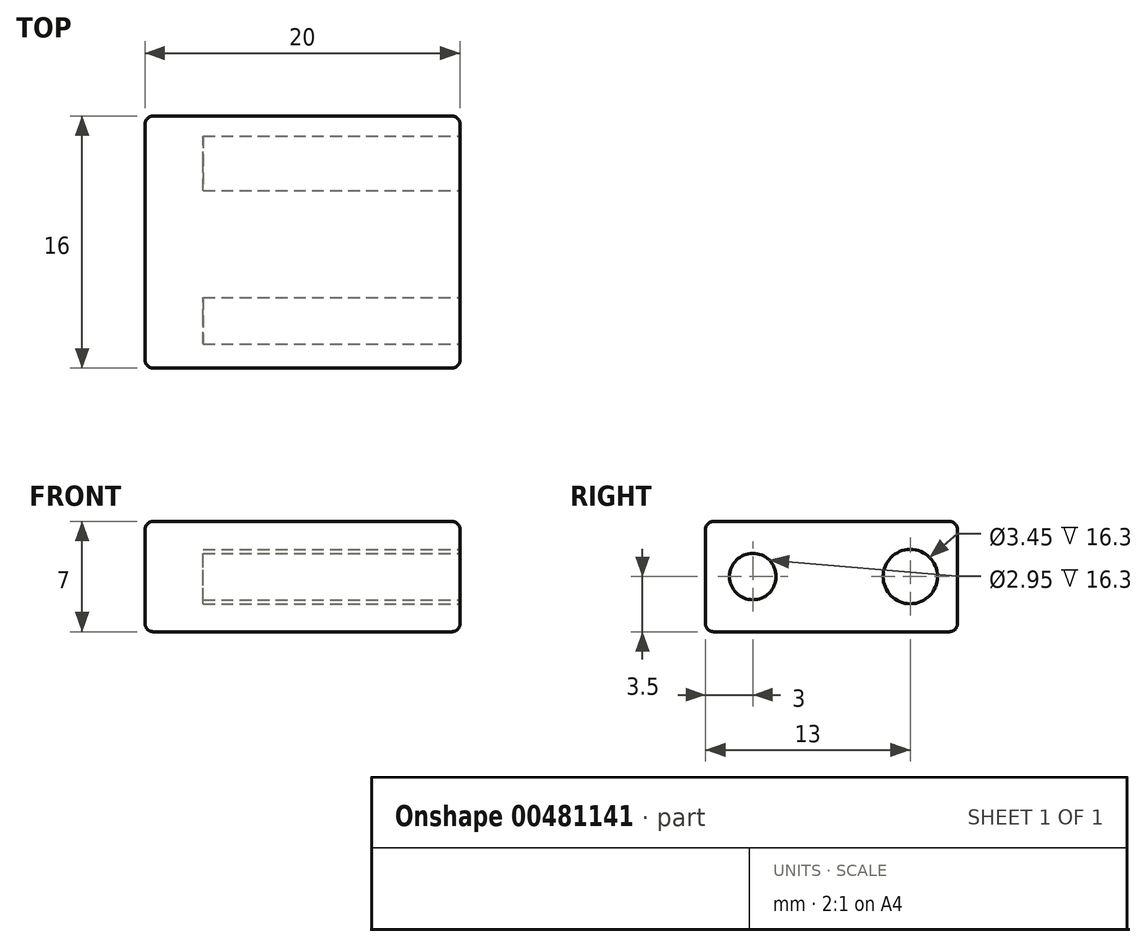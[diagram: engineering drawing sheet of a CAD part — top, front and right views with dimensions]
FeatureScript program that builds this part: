
annotation { "Feature Type Name" : "Feature", "Feature Type Description" : "" }
export const myFeature = defineFeature(function(context is Context, id is Id, definition is map)
    precondition{}
    {
        {
            var Q0;
            Q0=qCreatedBy(makeId("Top.planeOp"),FACE);
            var sketch = newSketch(context, id + "F0", { "sketchPlane" : qUnion([Q0])});
            skLineSegment(sketch, "E0.bottom", {"start": v(-10, 8) * mm, "end": v(10, 8) * mm});
            skLineSegment(sketch, "E0.top", {"start": v(-10, -8) * mm, "end": v(10, -8) * mm});
            skLineSegment(sketch, "E0.left", {"start": v(-10, 8) * mm, "end": v(-10, -8) * mm});
            skLineSegment(sketch, "E0.right", {"start": v(10, 8) * mm, "end": v(10, -8) * mm});
            skSolve(sketch);
        }
        {
            var Q0;
            Q0=makeQuery(id+"F0.imprint","IMPRINT",FACE,{"disambiguationData":[TD([[makeQuery(id+"F0.imprint","IMPRINT",EDGE,{"derivedFrom":sQuery(id+"F0.wireOp",EDGE,"E0.bottom")}),-1.0]])]});
            extrude(context, id + "F1", {"entities" : qUnion([Q0]), "oppositeDirection" : true, "depth" : 7 * mm});
        }
        {
            var Q0;
            Q0=makeQuery(id+"F1.opExtrude","CAP_FACE",FACE,{"disambiguationData":[OSD([sQuery(id+"F0.wireOp",EDGE,"E0.bottom"),sQuery(id+"F0.wireOp",EDGE,"E0.top"),sQuery(id+"F0.wireOp",EDGE,"E0.left"),sQuery(id+"F0.wireOp",EDGE,"E0.right")])],"isStart":true});
            var Q1;
            Q1=makeQuery(id+"F1.opExtrude","CAP_EDGE",EDGE,{"disambiguationData":[OSD([sQuery(id+"F0.wireOp",EDGE,"E0.top")])],"isStart":false});
            fillet(context, id + "F2", {"entities" : qUnion([Q0, Q1]), "radius" : 0.5 * mm, "tangentPropagation" : true, "allowEdgeOverflow" : false});
        }
        {
            var Q0;
            Q0=makeQuery(id+"F1.opExtrude","CAP_EDGE",EDGE,{"disambiguationData":[OSD([sQuery(id+"F0.wireOp",EDGE,"E0.bottom")])],"isStart":false});
            var Q1;
            Q1=makeQuery(id+"F1.opExtrude","CAP_FACE",FACE,{"disambiguationData":[OSD([sQuery(id+"F0.wireOp",EDGE,"E0.bottom"),sQuery(id+"F0.wireOp",EDGE,"E0.top"),sQuery(id+"F0.wireOp",EDGE,"E0.left"),sQuery(id+"F0.wireOp",EDGE,"E0.right")])],"isStart":false});
            fillet(context, id + "F3", {"entities" : qUnion([Q0, Q1]), "radius" : 0.5 * mm, "tangentPropagation" : true, "allowEdgeOverflow" : false});
        }
        {
            var Q0;
            Q0=makeQuery(id+"F1.opExtrude","SWEPT_EDGE",EDGE,{"disambiguationData":[OSD([sQuery(id+"F0.wireOp",EDGE,"E0.bottom"),sQuery(id+"F0.wireOp",EDGE,"E0.left")])]});
            fillet(context, id + "F4", {"entities" : qUnion([Q0]), "radius" : 0.5 * mm, "tangentPropagation" : true, "allowEdgeOverflow" : false});
        }
        {
            var Q0;
            Q0=makeQuery(id+"F1.opExtrude","SWEPT_EDGE",EDGE,{"disambiguationData":[OSD([sQuery(id+"F0.wireOp",EDGE,"E0.bottom"),sQuery(id+"F0.wireOp",EDGE,"E0.right")])]});
            fillet(context, id + "F5", {"entities" : qUnion([Q0]), "radius" : 0.5 * mm, "tangentPropagation" : true, "allowEdgeOverflow" : false});
        }
        {
            var Q0;
            Q0=makeQuery(id+"F1.opExtrude","SWEPT_FACE",FACE,{"disambiguationData":[OSD([sQuery(id+"F0.wireOp",EDGE,"E0.right")])]});
            var sketch = newSketch(context, id + "F6", { "sketchPlane" : qUnion([Q0])});
            skCircle(sketch, "E1", {"center": v(-5, -3.5) * mm, "radius": 1.48 * mm});
            skCircle(sketch, "E2", {"center": v(5, -3.5) * mm, "radius": 1.73 * mm});
            skSolve(sketch);
        }
        {
            var Q0;
            Q0 = qSketchRegion(id + "F6", true);
            extrude(context, id + "F7", {"entities" : qUnion([Q0]), "operationType" : NewBodyOperationType.REMOVE, "oppositeDirection" : true, "depth" : 16.3 * mm});
        }
    });
